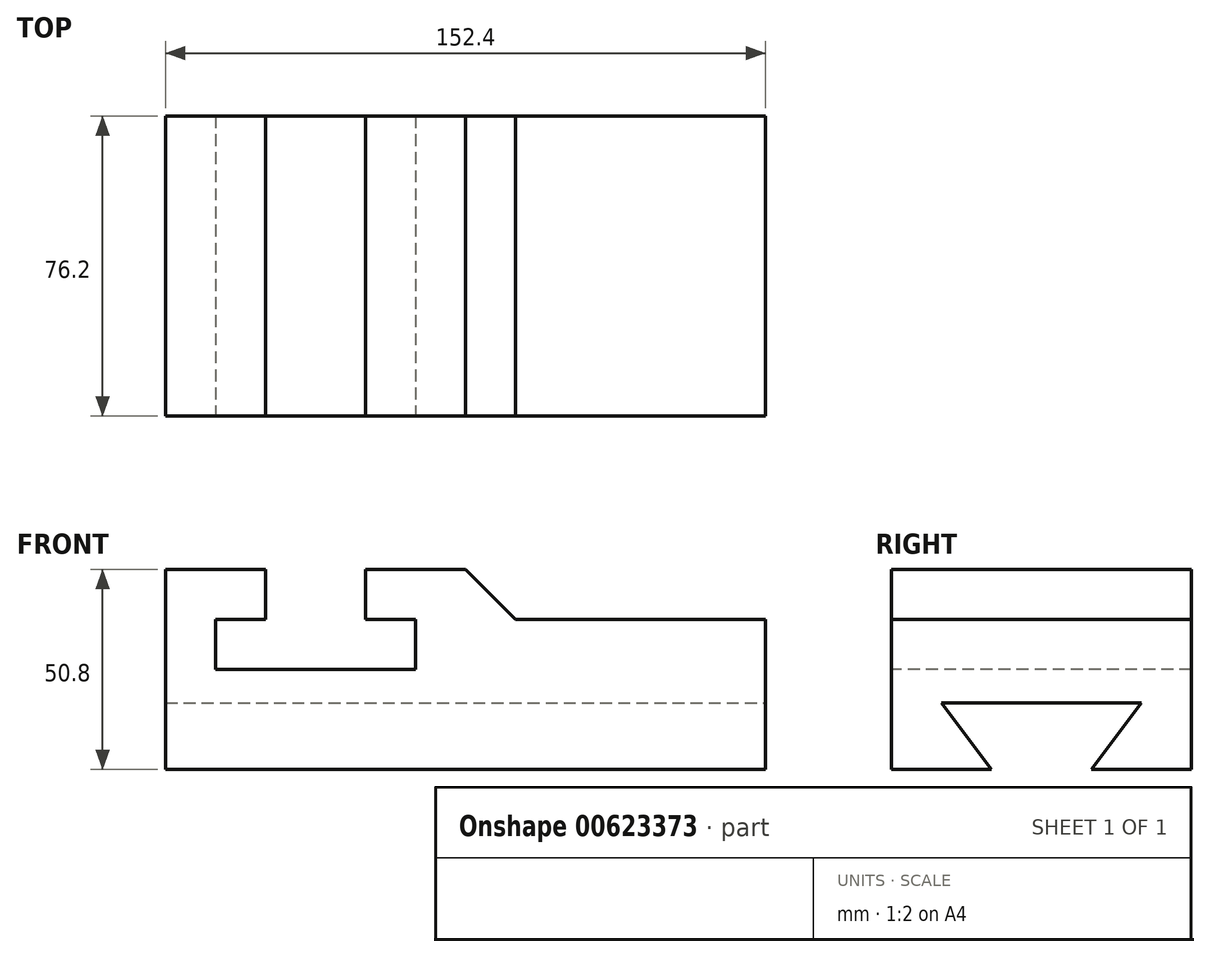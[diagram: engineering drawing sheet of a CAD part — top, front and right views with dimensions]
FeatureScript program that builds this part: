
annotation { "Feature Type Name" : "Feature", "Feature Type Description" : "" }
export const myFeature = defineFeature(function(context is Context, id is Id, definition is map)
    precondition{}
    {
        {
            var Q0;
            Q0=qCreatedBy(makeId("Front.planeOp"),FACE);
            var sketch = newSketch(context, id + "F0", { "sketchPlane" : qUnion([Q0])});
            skLineSegment(sketch, "E0", {"start": v(88.9, 38.1) * mm, "end": v(152.4, 38.1) * mm});
            skLineSegment(sketch, "E1", {"start": v(152.4, 38.1) * mm, "end": v(152.4, 0) * mm});
            skLineSegment(sketch, "E2", {"start": v(152.4, 0) * mm, "end": v(0, 0) * mm});
            skLineSegment(sketch, "E3", {"start": v(0, 0) * mm, "end": v(0, 50.8) * mm});
            skLineSegment(sketch, "E4", {"start": v(0, 50.8) * mm, "end": v(25.4, 50.8) * mm});
            skLineSegment(sketch, "E5", {"start": v(25.4, 50.8) * mm, "end": v(25.4, 38.1) * mm});
            skLineSegment(sketch, "E6", {"start": v(25.4, 38.1) * mm, "end": v(12.7, 38.1) * mm});
            skLineSegment(sketch, "E7", {"start": v(12.7, 38.1) * mm, "end": v(12.7, 25.4) * mm});
            skLineSegment(sketch, "E8", {"start": v(12.7, 25.4) * mm, "end": v(63.5, 25.4) * mm});
            skLineSegment(sketch, "E9", {"start": v(63.5, 25.4) * mm, "end": v(63.5, 38.1) * mm});
            skLineSegment(sketch, "E10", {"start": v(63.5, 38.1) * mm, "end": v(50.8, 38.1) * mm});
            skLineSegment(sketch, "E11", {"start": v(50.8, 38.1) * mm, "end": v(50.8, 50.8) * mm});
            skLineSegment(sketch, "E12", {"start": v(50.8, 50.8) * mm, "end": v(76.2, 50.8) * mm});
            skLineSegment(sketch, "E13", {"start": v(76.2, 50.8) * mm, "end": v(88.9, 38.1) * mm});
            skSolve(sketch);
        }
        {
            var Q0;
            Q0 = qSketchRegion(id + "F0", true);
            extrude(context, id + "F1", {"entities" : qUnion([Q0]), "oppositeDirection" : true, "depth" : 76.2 * mm, "offsetDistance" : 25.4 * mm});
        }
        {
            var Q0;
            Q0=qCreatedBy(makeId("Right.planeOp"),FACE);
            var sketch = newSketch(context, id + "F2", { "sketchPlane" : qUnion([Q0])});
            skLineSegment(sketch, "E14", {"start": v(25.4, 0) * mm, "end": v(12.7, 12.7) * mm});
            skLineSegment(sketch, "E15", {"start": v(12.7, 12.7) * mm, "end": v(63.5, 12.7) * mm});
            skLineSegment(sketch, "E16", {"start": v(63.5, 12.7) * mm, "end": v(50.8, 0) * mm});
            skLineSegment(sketch, "E17", {"start": v(50.8, 0) * mm, "end": v(25.4, 0) * mm});
            skSolve(sketch);
        }
        {
            var Q0;
            Q0 = qSketchRegion(id + "F2", true);
            extrude(context, id + "F3", {"entities" : qUnion([Q0]), "operationType" : NewBodyOperationType.ADD, "depth" : 152.4 * mm, "offsetDistance" : 25.4 * mm});
        }
        {
            var Q0;
            Q0=makeQuery(id+"F1.opExtrude","SWEPT_FACE",FACE,{"disambiguationData":[OSD([sQuery(id+"F0.wireOp",EDGE,"E1")])]});
            var sketch = newSketch(context, id + "F4", { "sketchPlane" : qUnion([Q0])});
            skLineSegment(sketch, "E18", {"start": v(25.4, 0) * mm, "end": v(12.7, 11.4) * mm});
            skLineSegment(sketch, "E19", {"start": v(12.7, 11.4) * mm, "end": v(63.5, 11.4) * mm});
            skLineSegment(sketch, "E20", {"start": v(63.5, 11.4) * mm, "end": v(50.8, 0) * mm});
            skLineSegment(sketch, "E21", {"start": v(50.8, 0) * mm, "end": v(25.4, 0) * mm});
            skSolve(sketch);
        }
        {
            var Q0;
            Q0 = qSketchRegion(id + "F4", true);
            extrude(context, id + "F5", {"entities" : qUnion([Q0]), "operationType" : NewBodyOperationType.ADD, "oppositeDirection" : true, "depth" : 152.4 * mm, "offsetDistance" : 25.4 * mm});
        }
        {
            var Q0;
            Q0=makeQuery(id+"F1.opExtrude","SWEPT_FACE",FACE,{"disambiguationData":[OSD([sQuery(id+"F0.wireOp",EDGE,"E1")])]});
            var sketch = newSketch(context, id + "F6", { "sketchPlane" : qUnion([Q0])});
            skLineSegment(sketch, "E22", {"start": v(25.4, 0) * mm, "end": v(12.7, 16.9) * mm});
            skLineSegment(sketch, "E23", {"start": v(12.7, 16.9) * mm, "end": v(63.5, 16.9) * mm});
            skLineSegment(sketch, "E24", {"start": v(63.5, 16.9) * mm, "end": v(50.8, 0) * mm});
            skLineSegment(sketch, "E25", {"start": v(50.8, 0) * mm, "end": v(25.4, 0) * mm});
            skSolve(sketch);
        }
        {
            var Q0;
            Q0=makeQuery(id+"F6.imprint","IMPRINT",FACE,{"disambiguationData":[TD([[makeQuery(id+"F6.imprint","IMPRINT",EDGE,{"derivedFrom":sQuery(id+"F6.wireOp",EDGE,"E22")}),-1.0]])]});
            extrude(context, id + "F7", {"entities" : qUnion([Q0]), "operationType" : NewBodyOperationType.REMOVE, "oppositeDirection" : true, "depth" : 152.4 * mm, "offsetDistance" : 25.4 * mm});
        }
    });
